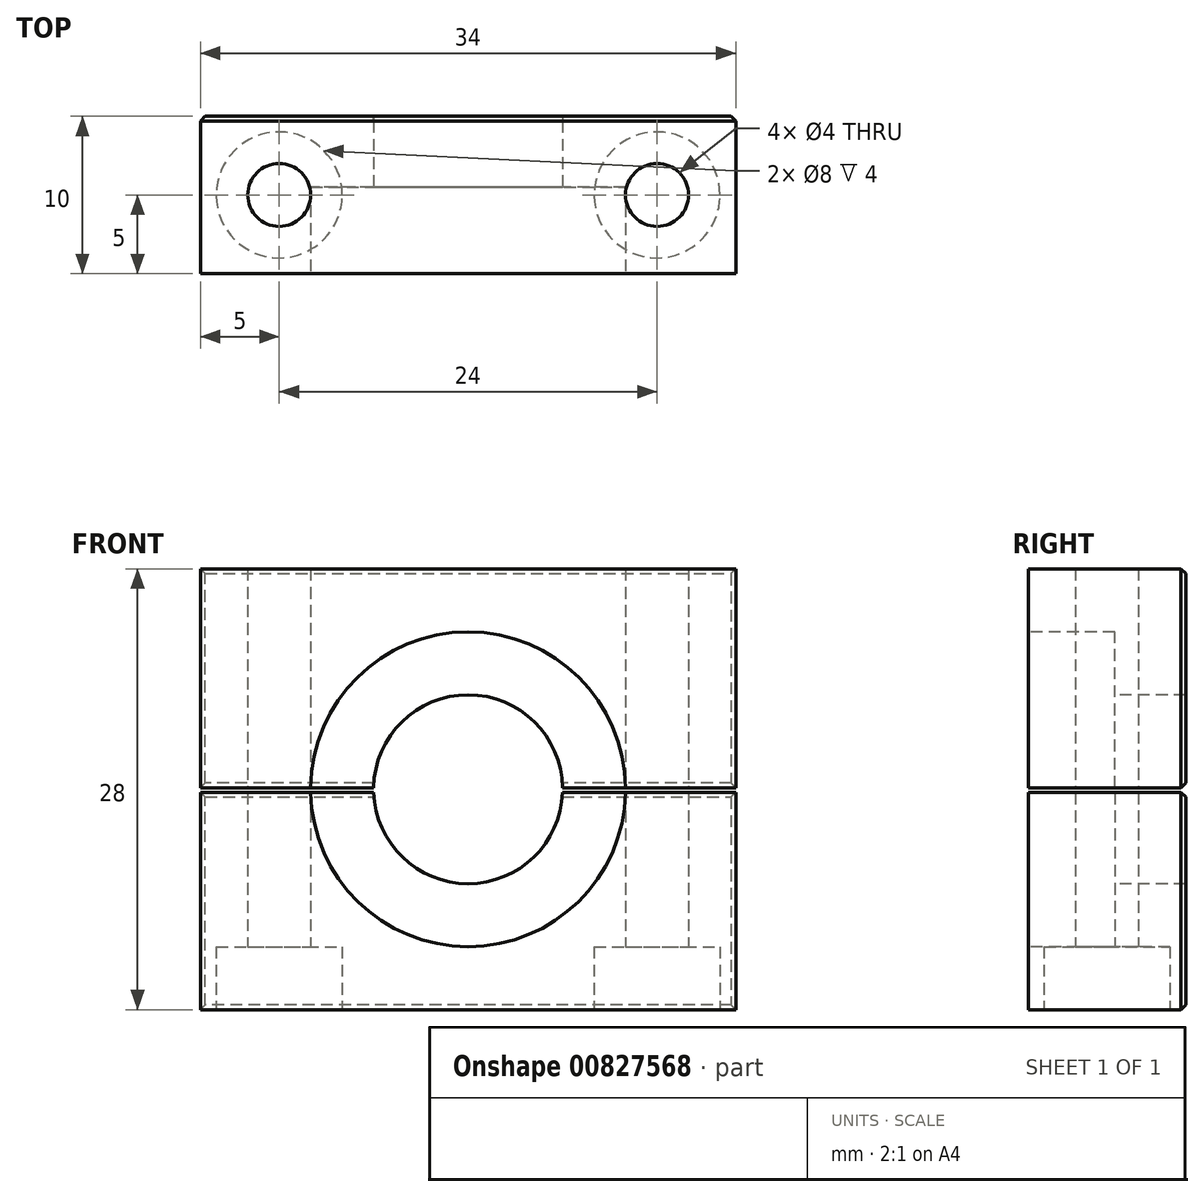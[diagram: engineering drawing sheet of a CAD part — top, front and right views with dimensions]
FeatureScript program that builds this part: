
annotation { "Feature Type Name" : "Feature", "Feature Type Description" : "" }
export const myFeature = defineFeature(function(context is Context, id is Id, definition is map)
    precondition{}
    {
        {
            var Q0;
            Q0=qCreatedBy(makeId("Front.planeOp"),FACE);
            var sketch = newSketch(context, id + "F0", { "sketchPlane" : qUnion([Q0])});
            skPoint(sketch, "E0.middle", {"position": v(0, 0) * mm});
            skLineSegment(sketch, "E1.bottom", {"start": v(-17, 14) * mm, "end": v(17, 14) * mm});
            skLineSegment(sketch, "E1.top", {"start": v(-17, -14) * mm, "end": v(17, -14) * mm});
            skLineSegment(sketch, "E1.left", {"start": v(-17, 14) * mm, "end": v(-17, -14) * mm});
            skLineSegment(sketch, "E1.right", {"start": v(17, 14) * mm, "end": v(17, -14) * mm});
            skLineSegment(sketch, "E2", {"start": v(-23.27, 0) * mm, "end": v(25.57, 0) * mm});
            skLineSegment(sketch, "E3.0", {"start": v(-23.27, -0.2) * mm, "end": v(25.57, -0.2) * mm});
            skLineSegment(sketch, "E4.0", {"start": v(-23.27, 0.1) * mm, "end": v(25.57, 0.1) * mm});
            skSolve(sketch);
        }
        {
            var Q0;
            Q0=makeQuery(id+"F0.imprint","IMPRINT",FACE,{"disambiguationData":[TD([[makeQuery(id+"F0.imprint","IMPRINT",EDGE,{"derivedFrom":sQuery(id+"F0.wireOp",EDGE,"E0.bottom")}),-1.0]])]});
            var Q1;
            Q1=makeQuery(id+"F0.imprint","IMPRINT",FACE,{"disambiguationData":[TD([[makeQuery(id+"F0.imprint","IMPRINT",EDGE,{"derivedFrom":sQuery(id+"F0.wireOp",EDGE,"E1.bottom")}),-1.0]])]});
            var Q2;
            {var subQ5=sQuery(id+"F0.wireOp",EDGE,"E1.top");Q2=makeQuery(id+"F0.imprint","IMPRINT",FACE,{"disambiguationData":[TD([[makeQuery(id+"F0.imprint","IMPRINT",EDGE,{"derivedFrom":subQ5}),1.0]])]});}
            extrude(context, id + "F1", {"entities" : qUnion([Q0, Q1, Q2]), "oppositeDirection" : true, "depth" : 10 * mm, "offsetDistance" : 25 * mm});
        }
        {
            var Q0;
            Q0=sQuery(id+"F0.wireOp",VERTEX,"E0.middle");
            var Q1;
            Q1=makeQuery(id+"F1.opExtrude","SWEPT_BODY",BODY,{"disambiguationData":[OSD([sQuery(id+"F0.wireOp",EDGE,"E1.bottom"),sQuery(id+"F0.wireOp",EDGE,"E1.left"),sQuery(id+"F0.wireOp",EDGE,"E1.right"),sQuery(id+"F0.wireOp",EDGE,"E4.0")])]});
            var Q2;
            Q2=makeQuery(id+"F1.opExtrude","SWEPT_BODY",BODY,{"disambiguationData":[OSD([sQuery(id+"F0.wireOp",EDGE,"E1.top"),sQuery(id+"F0.wireOp",EDGE,"E1.left"),sQuery(id+"F0.wireOp",EDGE,"E1.right"),sQuery(id+"F0.wireOp",EDGE,"E3.0")])]});
            hole(context, id + "F2", {"style" : HoleStyle.C_BORE, "endStyle" : HoleEndStyle.THROUGH, "holeDiameter" : 12 * mm, "cBoreDiameter" : 20 * mm, "cBoreDepth" : 5.5 * mm, "majorDiameter" : 5 * mm, "isTappedThrough" : true, "tappedDepth" : 8 * mm, "tapClearance" : 3, "locations" : qUnion([Q0]), "scope" : qUnion([Q1, Q2])});
        }
        {
            var Q0;
            Q0=makeQuery(id+"F1.opExtrude","SWEPT_FACE",FACE,{"disambiguationData":[OSD([sQuery(id+"F0.wireOp",EDGE,"E1.top")])]});
            var sketch = newSketch(context, id + "F3", { "sketchPlane" : qUnion([Q0])});
            skLineSegment(sketch, "E5.bottom", {"start": v(17, 0) * mm, "end": v(-17, 0) * mm});
            skLineSegment(sketch, "E5.top", {"start": v(17, -10) * mm, "end": v(-17, -10) * mm});
            skLineSegment(sketch, "E5.left", {"start": v(17, 0) * mm, "end": v(17, -10) * mm});
            skLineSegment(sketch, "E5.right", {"start": v(-17, 0) * mm, "end": v(-17, -10) * mm});
            skLineSegment(sketch, "E6.0", {"start": v(-12, 0) * mm, "end": v(-12, -10) * mm, "construction": true});
            skLineSegment(sketch, "E7.0", {"start": v(12, 0) * mm, "end": v(12, -10) * mm, "construction": true});
            skLineSegment(sketch, "E8.0", {"start": v(17, -5) * mm, "end": v(-17, -5) * mm, "construction": true});
            skPoint(sketch, "E9", {"position": v(-12, -5) * mm});
            skPoint(sketch, "E10", {"position": v(12, -5) * mm});
            skSolve(sketch);
        }
        {
            var Q0;
            Q0=sQuery(id+"F3.wireOp",VERTEX,"E9");
            var Q1;
            Q1=sQuery(id+"F3.wireOp",VERTEX,"E10");
            var Q2;
            Q2=makeQuery(id+"F1.opExtrude","SWEPT_BODY",BODY,{"disambiguationData":[OSD([sQuery(id+"F0.wireOp",EDGE,"E1.bottom"),sQuery(id+"F0.wireOp",EDGE,"E1.left"),sQuery(id+"F0.wireOp",EDGE,"E1.right"),sQuery(id+"F0.wireOp",EDGE,"E4.0")])]});
            var Q3;
            Q3=makeQuery(id+"F1.opExtrude","SWEPT_BODY",BODY,{"disambiguationData":[OSD([sQuery(id+"F0.wireOp",EDGE,"E1.top"),sQuery(id+"F0.wireOp",EDGE,"E1.left"),sQuery(id+"F0.wireOp",EDGE,"E1.right"),sQuery(id+"F0.wireOp",EDGE,"E3.0")])]});
            hole(context, id + "F4", {"style" : HoleStyle.C_BORE, "endStyle" : HoleEndStyle.THROUGH, "holeDiameter" : 4 * mm, "cBoreDiameter" : 8 * mm, "cBoreDepth" : 4 * mm, "majorDiameter" : 5 * mm, "isTappedThrough" : true, "tappedDepth" : 8 * mm, "tapClearance" : 3, "locations" : qUnion([Q0, Q1]), "scope" : qUnion([Q2, Q3])});
        }
        {
            var Q0;
            Q0=makeQuery(id+"F1.opExtrude","CAP_EDGE",EDGE,{"disambiguationData":[OSD([sQuery(id+"F0.wireOp",EDGE,"E1.bottom")])],"isStart":false});
            var Q1;
            {var subQ0=sQuery(id+"F0.wireOp",EDGE,"E1.left");Q1=makeQuery(id+"F1.opExtrude","CAP_EDGE",EDGE,{"disambiguationData":[OSD([subQ0]),TDD([makeQuery(id+"F0.imprint","IMPRINT",EDGE,{"disambiguationData":[TD([[makeQuery(id+"F0.imprint","INTERSECT",VERTEX,{"derivedFrom":[sQuery(id+"F0.wireOp",EDGE,"E1.bottom"),subQ0]}),-1.0]])],"derivedFrom":subQ0})])],"isStart":false});}
            var Q2;
            {var subQ0=sQuery(id+"F0.wireOp",EDGE,"E1.left");Q2=makeQuery(id+"F1.opExtrude","CAP_EDGE",EDGE,{"disambiguationData":[OSD([subQ0]),TDD([makeQuery(id+"F0.imprint","IMPRINT",EDGE,{"disambiguationData":[TD([[makeQuery(id+"F0.imprint","INTERSECT",VERTEX,{"derivedFrom":[sQuery(id+"F0.wireOp",EDGE,"E1.top"),subQ0]}),1.0]])],"derivedFrom":subQ0})])],"isStart":false});}
            var Q3;
            {var subQ0=sQuery(id+"F0.wireOp",EDGE,"E1.right");Q3=makeQuery(id+"F1.opExtrude","CAP_EDGE",EDGE,{"disambiguationData":[OSD([subQ0]),TDD([makeQuery(id+"F0.imprint","IMPRINT",EDGE,{"disambiguationData":[TD([[makeQuery(id+"F0.imprint","INTERSECT",VERTEX,{"derivedFrom":[sQuery(id+"F0.wireOp",EDGE,"E1.top"),subQ0]}),1.0]])],"derivedFrom":subQ0})])],"isStart":false});}
            var Q4;
            {var subQ0=sQuery(id+"F0.wireOp",EDGE,"E1.right");Q4=makeQuery(id+"F1.opExtrude","CAP_EDGE",EDGE,{"disambiguationData":[OSD([subQ0]),TDD([makeQuery(id+"F0.imprint","IMPRINT",EDGE,{"disambiguationData":[TD([[makeQuery(id+"F0.imprint","INTERSECT",VERTEX,{"derivedFrom":[sQuery(id+"F0.wireOp",EDGE,"E1.bottom"),subQ0]}),-1.0]])],"derivedFrom":subQ0})])],"isStart":false});}
            var Q5;
            Q5=makeQuery(id+"F1.opExtrude","CAP_EDGE",EDGE,{"disambiguationData":[OSD([sQuery(id+"F0.wireOp",EDGE,"E1.top")])],"isStart":false});
            var Q6;
            {var subQ0=sQuery(id+"F0.wireOp",EDGE,"E3.0");var subQ1=sQuery(id+"F0.wireOp",EDGE,"E1.left");var subQ2=sQuery(id+"F0.wireOp",EDGE,"E1.top");Q6=makeQuery(id+"F2.hole-0.boolean.opBoolean","SPLIT",EDGE,{"disambiguationData":[TD([makeQuery(id+"F1.opExtrude","SWEPT_FACE",FACE,{"disambiguationData":[OSD([subQ1]),TDD([makeQuery(id+"F0.imprint","IMPRINT",EDGE,{"disambiguationData":[TD([[makeQuery(id+"F0.imprint","INTERSECT",VERTEX,{"derivedFrom":[subQ2,subQ1]}),1.0]])],"derivedFrom":subQ1})])]})])],"derivedFrom":makeQuery(id+"F1.opExtrude","CAP_EDGE",EDGE,{"disambiguationData":[OSD([subQ0])],"isStart":false})});}
            var Q7;
            {var subQ0=sQuery(id+"F0.wireOp",EDGE,"E4.0");var subQ1=sQuery(id+"F0.wireOp",EDGE,"E1.right");var subQ2=sQuery(id+"F0.wireOp",EDGE,"E1.bottom");Q7=makeQuery(id+"F2.hole-0.boolean.opBoolean","SPLIT",EDGE,{"disambiguationData":[TD([makeQuery(id+"F1.opExtrude","SWEPT_FACE",FACE,{"disambiguationData":[OSD([subQ1]),TDD([makeQuery(id+"F0.imprint","IMPRINT",EDGE,{"disambiguationData":[TD([[makeQuery(id+"F0.imprint","INTERSECT",VERTEX,{"derivedFrom":[subQ2,subQ1]}),-1.0]])],"derivedFrom":subQ1})])]})])],"derivedFrom":makeQuery(id+"F1.opExtrude","CAP_EDGE",EDGE,{"disambiguationData":[OSD([subQ0])],"isStart":false})});}
            var Q8;
            {var subQ0=sQuery(id+"F0.wireOp",EDGE,"E3.0");var subQ1=sQuery(id+"F0.wireOp",EDGE,"E1.right");var subQ2=sQuery(id+"F0.wireOp",EDGE,"E1.top");Q8=makeQuery(id+"F2.hole-0.boolean.opBoolean","SPLIT",EDGE,{"disambiguationData":[TD([makeQuery(id+"F1.opExtrude","SWEPT_FACE",FACE,{"disambiguationData":[OSD([subQ1]),TDD([makeQuery(id+"F0.imprint","IMPRINT",EDGE,{"disambiguationData":[TD([[makeQuery(id+"F0.imprint","INTERSECT",VERTEX,{"derivedFrom":[subQ2,subQ1]}),1.0]])],"derivedFrom":subQ1})])]})])],"derivedFrom":makeQuery(id+"F1.opExtrude","CAP_EDGE",EDGE,{"disambiguationData":[OSD([subQ0])],"isStart":false})});}
            var Q9;
            {var subQ0=sQuery(id+"F0.wireOp",EDGE,"E4.0");var subQ1=sQuery(id+"F0.wireOp",EDGE,"E1.left");var subQ2=sQuery(id+"F0.wireOp",EDGE,"E1.bottom");Q9=makeQuery(id+"F2.hole-0.boolean.opBoolean","SPLIT",EDGE,{"disambiguationData":[TD([makeQuery(id+"F1.opExtrude","SWEPT_FACE",FACE,{"disambiguationData":[OSD([subQ1]),TDD([makeQuery(id+"F0.imprint","IMPRINT",EDGE,{"disambiguationData":[TD([[makeQuery(id+"F0.imprint","INTERSECT",VERTEX,{"derivedFrom":[subQ2,subQ1]}),-1.0]])],"derivedFrom":subQ1})])]})])],"derivedFrom":makeQuery(id+"F1.opExtrude","CAP_EDGE",EDGE,{"disambiguationData":[OSD([subQ0])],"isStart":false})});}
            chamfer(context, id + "F5", {"entities" : qUnion([Q0, Q1, Q2, Q3, Q4, Q5, Q6, Q7, Q8, Q9]), "width" : 0.3 * mm, "tangentPropagation" : true});
        }
    });
